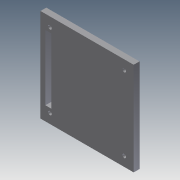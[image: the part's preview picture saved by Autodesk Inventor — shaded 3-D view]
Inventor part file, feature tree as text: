
AUTODESK INVENTOR PART (.ipt)
format: ipt  version: 2011 (Build 150239000, 239)  size: 537,600 bytes
history: native  units: in
note: dims shown in document units (in); Inventor stores cm internally (conversion verified against a paired STEP export)
features: extrude x52, sketch x52, fillet x2
ambient origin geometry x8: Origin, YZ Plane, XZ Plane, XY Plane, X Axis, Y Axis, Z Axis, Center Point
bodies: Solid1 (feature_tree)
feature tree (106):
  extrude  "Extrusion1"  Depth=4.0in
  extrude  "Extrusion2"  Depth=2.16in
  extrude  "Extrusion3"  Depth=1.7655in
  extrude  "Extrusion4"  Depth=0.029in TaperAngle=0.0deg
  extrude  "Extrusion5"  Depth=2.36in
  fillet  "Fillet1"  Radius=2.56in
  extrude  "Extrusion6"  Depth=0.125in
  extrude  "Extrusion7"  Depth=0.262in TaperAngle=0.0deg
  extrude  "Extrusion8"  Depth=0.029in TaperAngle=0.0deg
  extrude  "Extrusion9"  Depth=0.156in
  extrude  "Extrusion10"  Depth=0.5in TaperAngle=0.0deg
  extrude  "Extrusion11"  Depth=0.5in TaperAngle=0.0deg
  extrude  "Extrusion12"  Depth=1.875in TaperAngle=0.0deg
  extrude  "Extrusion13"  Depth=2.125in TaperAngle=0.0deg
  sketch  "Sketch14"  dims[d44=2.125in d45=0.0in d46=2.125in d47=0.0in]
  sketch  "Sketch15"  dims[d48=2.125in d49=0.0in d50=1.875in d51=0.0in]
  sketch  "Sketch16"  dims[d52=2.125in d53=0.0in d54=2.125in d55=0.0in]
  sketch  "Sketch17"  dims[d56=1.875in d57=0.0in d58=1.875in d59=0.0in]
  extrude  "Extrusion14"  Depth=2.125in TaperAngle=0.0deg
  extrude  "Extrusion15"  Depth=1.875in TaperAngle=0.0deg
  extrude  "Extrusion16"  Depth=2.125in TaperAngle=0.0deg
  extrude  "Extrusion17"  Depth=1.875in TaperAngle=0.0deg
  extrude  "Extrusion18"  Depth=2.125in TaperAngle=0.0deg
  extrude  "Extrusion19"  Depth=6.248in TaperAngle=0.0deg
  extrude  "Extrusion20"  Depth=1.281in
  extrude  "Extrusion21"  Depth=7.0in TaperAngle=0.0deg
  extrude  "Extrusion22"  Depth=2.0in
  extrude  "Extrusion23"  Depth=4.0in
  extrude  "Extrusion24"  Depth=2.0in
  extrude  "Extrusion25"  Depth=1.0in TaperAngle=0.0deg
  extrude  "Extrusion26"  Depth=0.25in
  extrude  "Extrusion27"  Depth=0.25in TaperAngle=0.0deg
  extrude  "Extrusion28"  Depth=0.25in TaperAngle=0.0deg
  extrude  "Extrusion29"  Depth=0.875in
  extrude  "Extrusion30"  Depth=0.5in TaperAngle=0.0deg
  extrude  "Extrusion31"  Depth=0.875in
  extrude  "Extrusion32"  Depth=0.5in TaperAngle=0.0deg
  extrude  "Extrusion33"  Depth=2.0in
  extrude  "Extrusion34"  Depth=4.0in
  fillet  "Fillet2"  Radius=1.0in
  extrude  "Extrusion35"  Depth=0.75in TaperAngle=0.0deg
  extrude  "Extrusion36"  Depth=0.9055in
  extrude  "Extrusion37"  Depth=0.8268in
  extrude  "Extrusion38"  Depth=0.75in TaperAngle=0.0deg
  extrude  "Extrusion39"  Depth=0.2559in
  extrude  "Extrusion40"  Depth=0.315in
  extrude  "Extrusion41"  Depth=1.063in
  extrude  "Extrusion42"  Depth=1.0in TaperAngle=0.0deg
  extrude  "Extrusion43"  Depth=0.406in
  extrude  "Extrusion44"  Depth=4.0in
  extrude  "Extrusion45"  Depth=0.21in
  extrude  "Extrusion46"  Depth=0.6in
  extrude  "Extrusion47"  Depth=0.25in TaperAngle=0.0deg
  extrude  "Extrusion48"  Depth=0.03in
  extrude  "Extrusion49"  Depth=0.6299in
  extrude  "Extrusion50"  Depth=0.0787in
  extrude  "Extrusion51"  Depth=0.0787in
  extrude  "Extrusion52"  [1 undecoded]
  sketch  "Sketch1"  dims[d0=4.0in d1=4.0in]
  sketch  "Sketch2"  dims[d2=0.029in d3=0.0in d4=2.16in]
  sketch  "Sketch3"  dims[d5=0.029in d6=0.0in d7=1.7655in]
  sketch  "Sketch4"  dims[d8=0.156in d9=0.029in d10=0.0in]
  sketch  "Sketch5"  dims[d11=0.029in d12=0.0in d13=2.36in d14=2.56in]
  sketch  "Sketch6"  dims[d15=0.262in d16=0.0in d17=0.125in]
  sketch  "Sketch7"  dims[d18=0.362in d19=0.0in d20=0.262in d21=0.0in]
  sketch  "Sketch8"  dims[d22=0.1in d23=0.0in d24=0.029in d25=0.0in]
  sketch  "Sketch9"  dims[d26=1.594in d27=0.156in]
  sketch  "Sketch10"  dims[d28=0.029in d29=0.0in d30=0.5in d31=0.0in]
  sketch  "Sketch11"  dims[d32=0.75in d33=0.0in d34=0.5in d35=0.0in]
  sketch  "Sketch12"  dims[d36=2.125in d37=0.0in d38=1.875in d39=0.0in]
  sketch  "Sketch13"  dims[d40=1.875in d41=0.0in d42=2.125in d43=0.0in]
  sketch  "Sketch18"  dims[d60=2.125in d61=0.0in d62=2.125in d63=0.0in]
  sketch  "Sketch19"  dims[d64=0.875in d65=0.0in d66=6.248in d67=0.0in]
  sketch  "Sketch20"  dims[d68=7.0in d69=0.0in d70=1.281in]
  sketch  "Sketch21"  dims[d71=3.188in d72=7.0in d73=0.0in]
  sketch  "Sketch22"  dims[d74=0.25in d75=0.0in d76=2.0in]
  sketch  "Sketch23"  dims[d77=2.0in d78=4.0in]
  sketch  "Sketch24"  dims[d79=1.0in d80=0.0in d81=2.0in]
  sketch  "Sketch25"  dims[d82=1.0in d83=1.0in d84=0.0in]
  sketch  "Sketch26"  dims[d85=0.5in d86=0.25in]
  sketch  "Sketch27"  dims[d87=0.25in d88=0.25in d89=0.0in]
  sketch  "Sketch28"  dims[d90=0.25in d91=0.0in d92=0.25in d93=0.0in]
  sketch  "Sketch29"  dims[d94=0.656in d95=0.875in]
  sketch  "Sketch30"  dims[d96=0.5in d97=0.0in d98=0.5in d99=0.0in]
  sketch  "Sketch31"  dims[d100=0.875in d101=0.875in]
  sketch  "Sketch32"  dims[d102=0.5in d103=0.0in d104=0.5in d105=0.0in]
  sketch  "Sketch33"  dims[d106=2.0in d107=2.0in]
  sketch  "Sketch34"  dims[d108=4.0in d109=4.0in d110=1.0in d111=0.0in]
  sketch  "Sketch35"  dims[d112=0.25in d113=0.0in d114=0.75in d115=0.0in]
  sketch  "Sketch36"  dims[d116=0.75in d117=0.0in d118=0.9055in]
  sketch  "Sketch37"  dims[d119=0.4134in d120=0.8268in]
  sketch  "Sketch38"  dims[d121=1.378in d122=0.75in d123=0.0in]
  sketch  "Sketch39"  dims[d124=0.5315in d125=0.2559in]
  sketch  "Sketch40"  dims[d126=0.315in d127=0.315in]
  sketch  "Sketch41"  dims[d128=1.063in d129=1.063in]
  sketch  "Sketch42"  dims[d130=0.0787in d131=1.0in d132=0.0in]
  sketch  "Sketch43"  dims[d133=0.25in d134=0.0in d135=0.406in]
  sketch  "Sketch44"  dims[d136=4.0in d137=4.0in]
  sketch  "Sketch45"  dims[d138=0.25in d139=0.0in d140=0.21in]
  sketch  "Sketch46"  dims[d141=0.25in d142=0.6in]
  sketch  "Sketch47"  dims[d143=2.8in d144=0.25in d145=0.0in]
  sketch  "Sketch48"  dims[d146=0.03in d147=0.03in]
  sketch  "Sketch49"  dims[d148=0.25in d149=0.0in d150=0.6299in]
  sketch  "Sketch50"  dims[d151=0.0787in d152=0.0787in]
  sketch  "Sketch51"  dims[d153=0.0787in d154=0.0787in]
  sketch  "Sketch52"  dims[d155=0.25in d156=0.0in]
note: 1 required parameter value undecoded (feature->parameter linkage not recoverable at this tier; creation-order binding heuristic only, values carry confidence <= 0.55)
